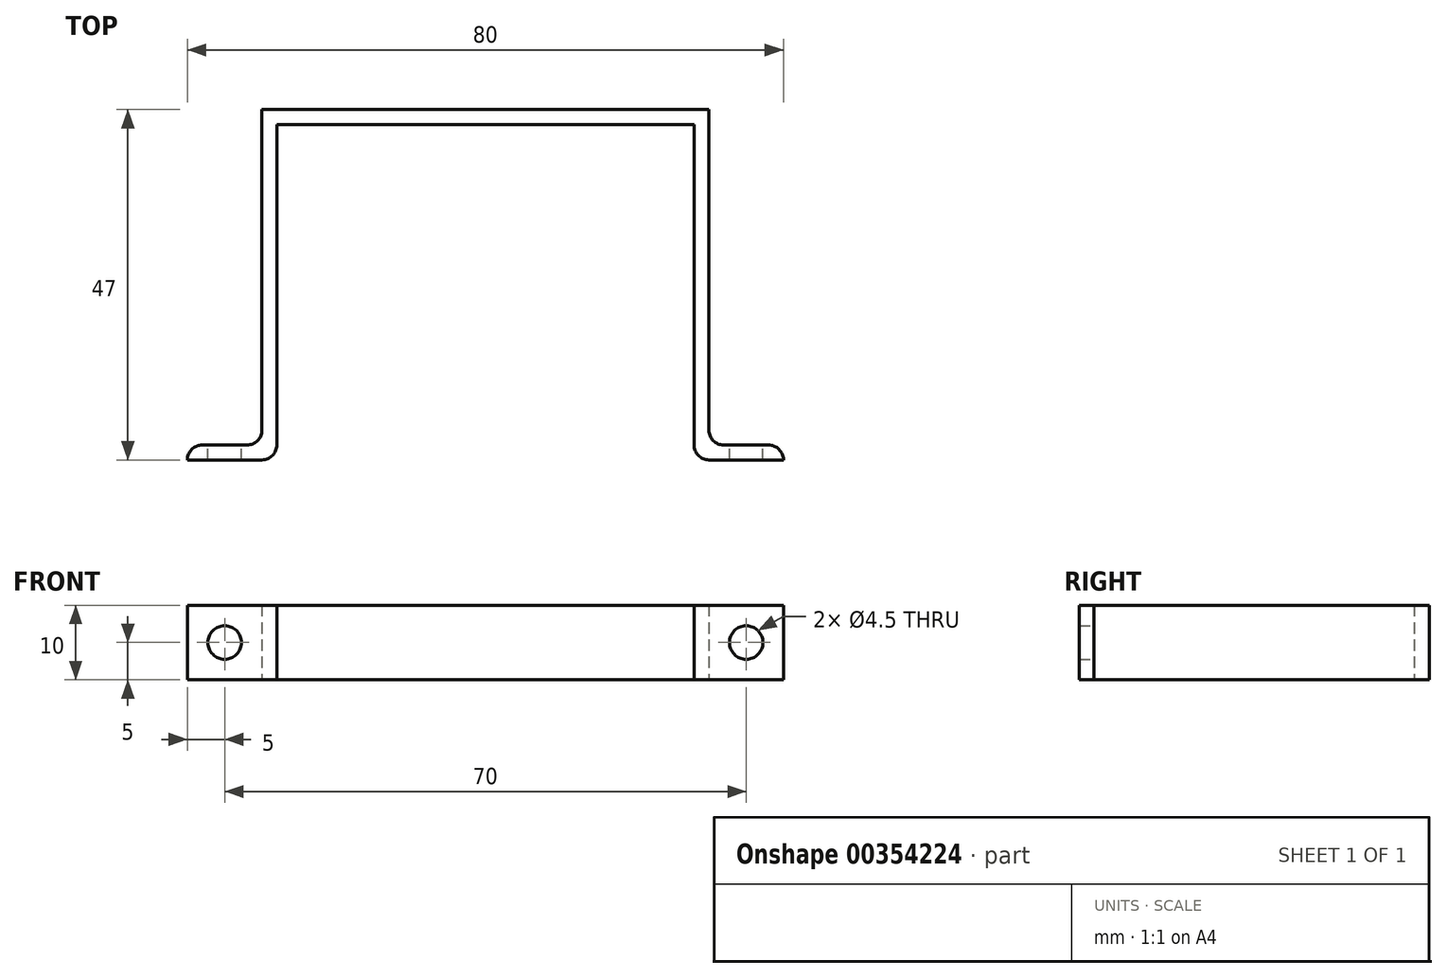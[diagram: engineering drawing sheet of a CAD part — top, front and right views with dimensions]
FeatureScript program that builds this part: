
annotation { "Feature Type Name" : "Feature", "Feature Type Description" : "" }
export const myFeature = defineFeature(function(context is Context, id is Id, definition is map)
    precondition{}
    {
        {
            var Q0;
            Q0=qCreatedBy(makeId("Top.planeOp"),FACE);
            var sketch = newSketch(context, id + "F0", { "sketchPlane" : qUnion([Q0])});
            skLineSegment(sketch, "E0", {"start": v(0, 45) * mm, "end": v(28, 45) * mm});
            skLineSegment(sketch, "E1", {"start": v(28, 45) * mm, "end": v(28, 0) * mm});
            skLineSegment(sketch, "E2", {"start": v(28, 0) * mm, "end": v(40, 0) * mm});
            skLineSegment(sketch, "E3", {"start": v(40, 0) * mm, "end": v(40, 2) * mm});
            skLineSegment(sketch, "E4", {"start": v(40, 2) * mm, "end": v(30, 2) * mm});
            skLineSegment(sketch, "E5", {"start": v(30, 2) * mm, "end": v(30, 47) * mm});
            skLineSegment(sketch, "E6", {"start": v(30, 47) * mm, "end": v(0, 47) * mm});
            skLineSegment(sketch, "E7", {"start": v(0, 47) * mm, "end": v(0, 45) * mm});
            skLineSegment(sketch, "E8", {"start": v(30, 2) * mm, "end": v(28, 2) * mm, "construction": true});
            skSolve(sketch);
        }
        {
            var Q0;
            Q0=makeQuery(id+"F0.imprint","IMPRINT",FACE,{"disambiguationData":[TD([[makeQuery(id+"F0.imprint","IMPRINT",EDGE,{"derivedFrom":sQuery(id+"F0.wireOp",EDGE,"E0")}),1.0]])]});
            extrude(context, id + "F1", {"entities" : qUnion([Q0]), "endBound" : BoundingType.SYMMETRIC, "depth" : 10 * mm});
        }
        {
            var Q0;
            Q0=makeQuery(id+"F1.opExtrude","SWEPT_FACE",FACE,{"disambiguationData":[OSD([sQuery(id+"F0.wireOp",EDGE,"E4")])]});
            var sketch = newSketch(context, id + "F2", { "sketchPlane" : qUnion([Q0])});
            skPoint(sketch, "E9", {"position": v(-35, 0) * mm});
            skPoint(sketch, "E9.positionSnap0", {"position": v(-35, -5) * mm});
            skSolve(sketch);
        }
        {
            var Q0;
            Q0=sQuery(id+"F2.wireOp",VERTEX,"E9");
            var Q1;
            Q1=makeQuery(id+"F1.opExtrude","SWEPT_BODY",BODY,{"disambiguationData":[OSD([sQuery(id+"F0.wireOp",EDGE,"E0"),sQuery(id+"F0.wireOp",EDGE,"E1"),sQuery(id+"F0.wireOp",EDGE,"E2"),sQuery(id+"F0.wireOp",EDGE,"E3"),sQuery(id+"F0.wireOp",EDGE,"E4"),sQuery(id+"F0.wireOp",EDGE,"E5"),sQuery(id+"F0.wireOp",EDGE,"E6"),sQuery(id+"F0.wireOp",EDGE,"E7")])]});
            hole(context, id + "F3", {"style" : HoleStyle.SIMPLE, "endStyle" : HoleEndStyle.THROUGH, "standardTappedOrClearance" : lookupTablePath({ "standard" : "ANSI", "fit" : "Normal (ASME)", "size" : "#8", "type" : "Clearance" }), "standardBlindInLast" : lookupTablePath({ "fit" : "Free", "standard" : "ANSI", "size" : "#8", "type" : "Clearance" }), "holeDiameter" : 4.5 * mm, "isTappedThrough" : true, "tappedDepth" : 12 * mm, "tapClearance" : 3, "locations" : qUnion([Q0]), "scope" : qUnion([Q1])});
        }
        {
            var Q0;
            Q0=makeQuery(id+"F1.opExtrude","SWEPT_EDGE",EDGE,{"disambiguationData":[OSD([sQuery(id+"F0.wireOp",EDGE,"E4"),sQuery(id+"F0.wireOp",EDGE,"E5")])]});
            var Q1;
            Q1=makeQuery(id+"F1.opExtrude","SWEPT_EDGE",EDGE,{"disambiguationData":[OSD([sQuery(id+"F0.wireOp",EDGE,"E1"),sQuery(id+"F0.wireOp",EDGE,"E2")])]});
            var Q2;
            Q2=makeQuery(id+"F1.opExtrude","SWEPT_EDGE",EDGE,{"disambiguationData":[OSD([sQuery(id+"F0.wireOp",EDGE,"E3"),sQuery(id+"F0.wireOp",EDGE,"E4")])]});
            fillet(context, id + "F4", {"entities" : qUnion([Q0, Q1, Q2]), "radius" : 2 * mm, "tangentPropagation" : true, "allowEdgeOverflow" : false});
        }
        {
            var Q0;
            Q0=makeQuery(id+"F1.opExtrude","SWEPT_BODY",BODY,{"disambiguationData":[OSD([sQuery(id+"F0.wireOp",EDGE,"E0"),sQuery(id+"F0.wireOp",EDGE,"E1"),sQuery(id+"F0.wireOp",EDGE,"E2"),sQuery(id+"F0.wireOp",EDGE,"E3"),sQuery(id+"F0.wireOp",EDGE,"E4"),sQuery(id+"F0.wireOp",EDGE,"E5"),sQuery(id+"F0.wireOp",EDGE,"E6"),sQuery(id+"F0.wireOp",EDGE,"E7")])]});
            var Q1;
            Q1=qCreatedBy(makeId("Right.planeOp"),FACE);
            mirror(context, id + "F5", {"operationType" : NewBodyOperationType.ADD, "entities" : qUnion([Q0]), "mirrorPlane" : qUnion([Q1])});
        }
    });
